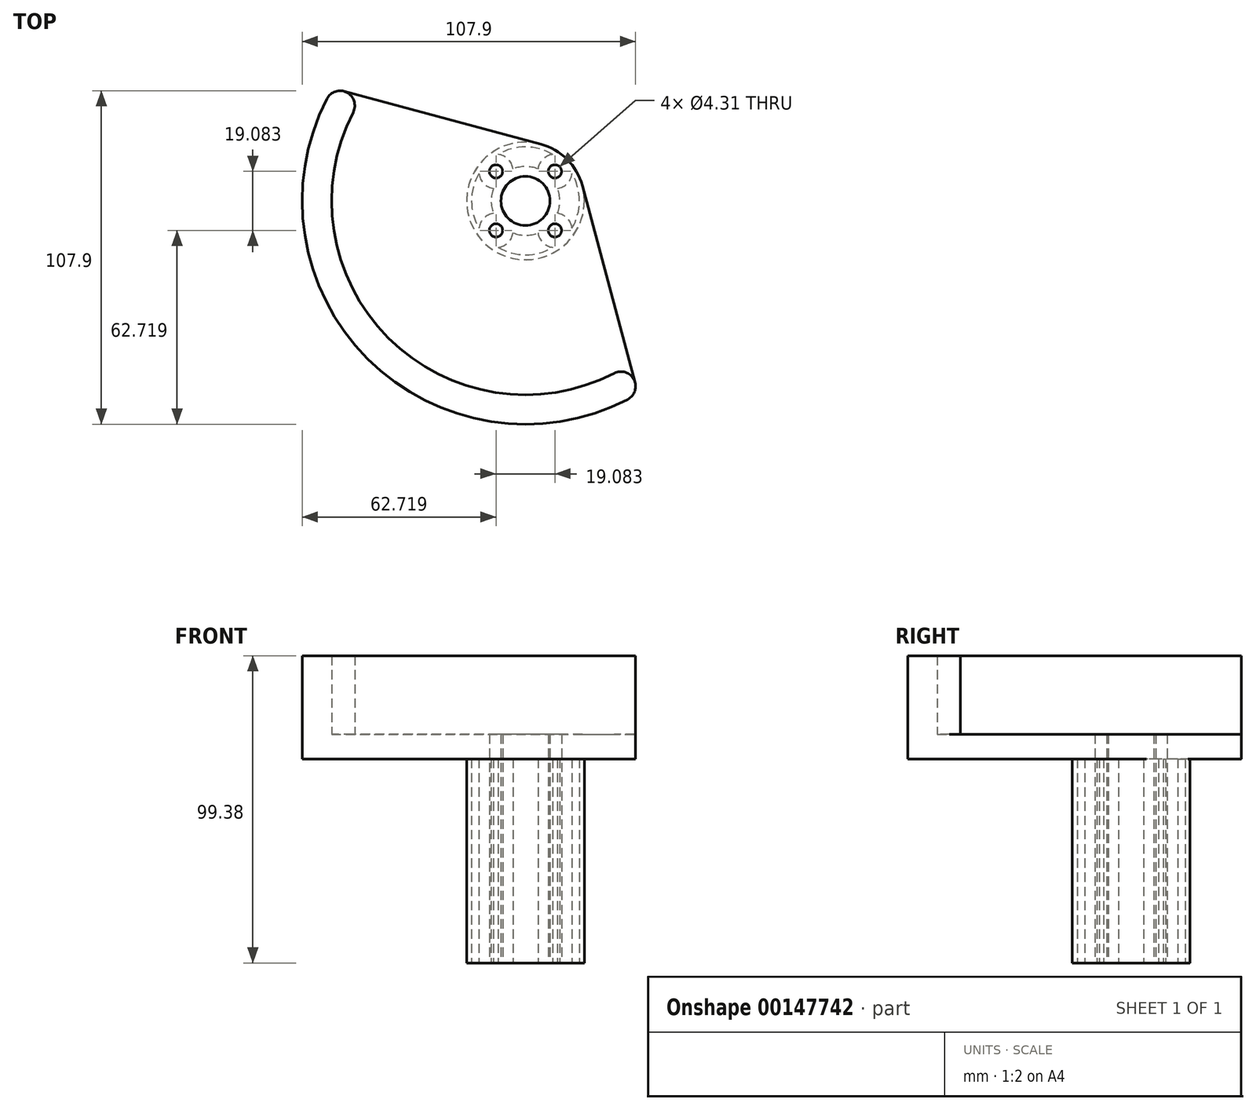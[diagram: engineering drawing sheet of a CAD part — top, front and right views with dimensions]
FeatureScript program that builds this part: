
annotation { "Feature Type Name" : "Feature", "Feature Type Description" : "" }
export const myFeature = defineFeature(function(context is Context, id is Id, definition is map)
    precondition{}
    {
        {
            var Q0;
            Q0=qCreatedBy(makeId("Top.planeOp"),FACE);
            var sketch = newSketch(context, id + "F0", { "sketchPlane" : qUnion([Q0])});
            skCircle(sketch, "E0", {"center": v(0, 0) * mm, "radius": 7.94 * mm});
            skLineSegment(sketch, "E1.bottom", {"start": v(9.54, 9.54) * mm, "end": v(-9.54, 9.54) * mm, "construction": true});
            skLineSegment(sketch, "E1.top", {"start": v(9.54, -9.54) * mm, "end": v(-9.54, -9.54) * mm, "construction": true});
            skLineSegment(sketch, "E1.left", {"start": v(9.54, 9.54) * mm, "end": v(9.54, -9.54) * mm, "construction": true});
            skLineSegment(sketch, "E1.right", {"start": v(-9.54, 9.54) * mm, "end": v(-9.54, -9.54) * mm, "construction": true});
            skCircle(sketch, "E2", {"center": v(-9.54, 9.54) * mm, "radius": 5.56 * mm, "construction": true});
            skLineSegment(sketch, "E3", {"start": v(0, 0) * mm, "end": v(0, 7.94) * mm});
            skCircle(sketch, "E4", {"center": v(-9.54, 9.54) * mm, "radius": 2.15 * mm});
            skCircle(sketch, "E5", {"center": v(-9.54, -9.54) * mm, "radius": 2.15 * mm});
            skCircle(sketch, "E6", {"center": v(9.54, -9.54) * mm, "radius": 2.15 * mm});
            skCircle(sketch, "E7", {"center": v(9.54, 9.54) * mm, "radius": 2.15 * mm});
            skCircle(sketch, "E8", {"center": v(0, 0) * mm, "radius": 19.05 * mm});
            skSolve(sketch);
        }
        {
            var Q0;
            Q0=qSketchRegion(id+"F0",true);
            extrude(context, id + "F1", {"entities" : qUnion([Q0]), "depth" : 66.04 * mm});
        }
        {
            var Q0;
            Q0=makeQuery(id+"F1.opExtrude","CAP_FACE",FACE,{"disambiguationData":[OSD([sQuery(id+"F0.wireOp",EDGE,"E0"),sQuery(id+"F0.wireOp",EDGE,"E4"),sQuery(id+"F0.wireOp",EDGE,"E5"),sQuery(id+"F0.wireOp",EDGE,"E6"),sQuery(id+"F0.wireOp",EDGE,"E7"),sQuery(id+"F0.wireOp",EDGE,"E8")])],"isStart":true});
            var sketch = newSketch(context, id + "F2", { "sketchPlane" : qUnion([Q0])});
            skArc(sketch, "E9", {"start": v(4.04, -10.35) * mm, "mid": v(5.65, -13.51) * mm, "end": v(8.85, -15.05) * mm});
            skArc(sketch, "E10", {"start": v(-8.85, -15.05) * mm, "mid": v(0, -17.46) * mm, "end": v(8.85, -15.05) * mm});
            skArc(sketch, "E11", {"start": v(-4.04, -10.35) * mm, "mid": v(0, -11.11) * mm, "end": v(4.04, -10.35) * mm});
            skArc(sketch, "E12", {"start": v(-8.85, -15.05) * mm, "mid": v(-5.65, -13.51) * mm, "end": v(-4.04, -10.35) * mm});
            skSolve(sketch);
        }
        {
            var Q0;
            Q0=qSketchRegion(id+"F2",true);
            var Q1;
            Q1=makeQuery(id+"F1.opExtrude","CAP_FACE",FACE,{"disambiguationData":[OSD([sQuery(id+"F0.wireOp",EDGE,"E0"),sQuery(id+"F0.wireOp",EDGE,"E4"),sQuery(id+"F0.wireOp",EDGE,"E5"),sQuery(id+"F0.wireOp",EDGE,"E6"),sQuery(id+"F0.wireOp",EDGE,"E7"),sQuery(id+"F0.wireOp",EDGE,"E8")])],"isStart":false});
            extrude(context, id + "F3", {"entities" : qUnion([Q0]), "operationType" : NewBodyOperationType.REMOVE, "endBound" : BoundingType.UP_TO_SURFACE, "oppositeDirection" : true, "endBoundEntityFace" : qUnion([Q1]), "depth" : 25.4 * mm});
        }
        {
            var Q0;
            Q0=makeQuery(id+"F3.boolean.opBoolean","COPY",FACE,{"derivedFrom":makeQuery(id+"F3.opExtrude","SWEPT_FACE",FACE,{"disambiguationData":[OSD([sQuery(id+"F2.wireOp",EDGE,"E10")])]})});
            var Q1;
            Q1=makeQuery(id+"F3.boolean.opBoolean","COPY",FACE,{"derivedFrom":makeQuery(id+"F3.opExtrude","SWEPT_FACE",FACE,{"disambiguationData":[OSD([sQuery(id+"F2.wireOp",EDGE,"E12")])]})});
            var Q2;
            Q2=makeQuery(id+"F3.boolean.opBoolean","COPY",FACE,{"derivedFrom":makeQuery(id+"F3.opExtrude","SWEPT_FACE",FACE,{"disambiguationData":[OSD([sQuery(id+"F2.wireOp",EDGE,"E11")])]})});
            var Q3;
            Q3=makeQuery(id+"F3.boolean.opBoolean","COPY",FACE,{"derivedFrom":makeQuery(id+"F3.opExtrude","SWEPT_FACE",FACE,{"disambiguationData":[OSD([sQuery(id+"F2.wireOp",EDGE,"E9")])]})});
            var Q4;
            Q4=makeQuery(id+"F1.opExtrude","SWEPT_FACE",FACE,{"disambiguationData":[OSD([sQuery(id+"F0.wireOp",EDGE,"E8")])]});
            circularPattern(context, id + "F4", {"patternType" : PatternType.FACE, "faces" : qUnion([Q0, Q1, Q2, Q3]), "axis" : qUnion([Q4]), "angle" : 90 * degree, "instanceCount" : 4});
        }
        {
            var Q0;
            Q0=makeQuery(id+"F1.opExtrude","CAP_FACE",FACE,{"disambiguationData":[OSD([sQuery(id+"F0.wireOp",EDGE,"E0"),sQuery(id+"F0.wireOp",EDGE,"E4"),sQuery(id+"F0.wireOp",EDGE,"E5"),sQuery(id+"F0.wireOp",EDGE,"E6"),sQuery(id+"F0.wireOp",EDGE,"E7"),sQuery(id+"F0.wireOp",EDGE,"E8")])],"isStart":false});
            var sketch = newSketch(context, id + "F5", { "sketchPlane" : qUnion([Q0])});
            skArc(sketch, "E13", {"start": v(18.4, 4.93) * mm, "mid": v(13.47, 13.47) * mm, "end": v(4.93, 18.4) * mm});
            skLineSegment(sketch, "E14", {"start": v(18.4, 4.93) * mm, "end": v(35.47, -58.79) * mm});
            skLineSegment(sketch, "E15", {"start": v(4.93, 18.4) * mm, "end": v(-58.79, 35.47) * mm});
            skLineSegment(sketch, "E16", {"start": v(4.93, 18.4) * mm, "end": v(-26.93, 18.4) * mm, "construction": true});
            skLineSegment(sketch, "E17", {"start": v(-26.93, 18.4) * mm, "end": v(-26.93, 26.94) * mm, "construction": true});
            skArc(sketch, "E18", {"start": v(-58.79, 35.47) * mm, "mid": v(-61.95, 35.23) * mm, "end": v(-64.25, 33.05) * mm});
            skArc(sketch, "E19", {"start": v(33.05, -64.25) * mm, "mid": v(35.23, -61.95) * mm, "end": v(35.47, -58.79) * mm});
            skArc(sketch, "E20", {"start": v(-64.25, 33.05) * mm, "mid": v(-51.1, -51.1) * mm, "end": v(33.05, -64.25) * mm});
            skLineSegment(sketch, "E21", {"start": v(18.4, 4.93) * mm, "end": v(18.4, -26.93) * mm, "construction": true});
            skLineSegment(sketch, "E22", {"start": v(18.4, -26.93) * mm, "end": v(26.94, -26.93) * mm, "construction": true});
            skCircle(sketch, "E23", {"center": v(-9.54, 9.54) * mm, "radius": 2.15 * mm});
            skCircle(sketch, "E24", {"center": v(9.54, 9.54) * mm, "radius": 2.15 * mm});
            skCircle(sketch, "E25", {"center": v(-9.54, -9.54) * mm, "radius": 2.15 * mm});
            skCircle(sketch, "E26", {"center": v(9.54, -9.54) * mm, "radius": 2.15 * mm});
            skCircle(sketch, "E27", {"center": v(0, 0) * mm, "radius": 7.94 * mm});
            skSolve(sketch);
        }
        {
            var Q0;
            Q0=qSketchRegion(id+"F5",true);
            extrude(context, id + "F6", {"entities" : qUnion([Q0]), "operationType" : NewBodyOperationType.ADD, "depth" : 7.94 * mm});
        }
        {
            var Q0;
            Q0=makeQuery(id+"F6.opExtrude","CAP_FACE",FACE,{"disambiguationData":[OSD([sQuery(id+"F5.wireOp",EDGE,"E13"),sQuery(id+"F5.wireOp",EDGE,"E14"),sQuery(id+"F5.wireOp",EDGE,"E15"),sQuery(id+"F5.wireOp",EDGE,"E18"),sQuery(id+"F5.wireOp",EDGE,"E19"),sQuery(id+"F5.wireOp",EDGE,"E20"),sQuery(id+"F5.wireOp",EDGE,"E23"),sQuery(id+"F5.wireOp",EDGE,"E24"),sQuery(id+"F5.wireOp",EDGE,"E25"),sQuery(id+"F5.wireOp",EDGE,"E26"),sQuery(id+"F5.wireOp",EDGE,"E27")])],"isStart":false});
            var sketch = newSketch(context, id + "F7", { "sketchPlane" : qUnion([Q0])});
            skArc(sketch, "E28", {"start": v(-64.25, 33.05) * mm, "mid": v(-51.1, -51.1) * mm, "end": v(33.05, -64.25) * mm});
            skArc(sketch, "E29", {"start": v(-55.78, 28.7) * mm, "mid": v(-57.84, 35.1) * mm, "end": v(-64.25, 33.05) * mm});
            skArc(sketch, "E30", {"start": v(33.05, -64.25) * mm, "mid": v(35.1, -57.84) * mm, "end": v(28.7, -55.78) * mm});
            skArc(sketch, "E31", {"start": v(-55.78, 28.7) * mm, "mid": v(-44.36, -44.36) * mm, "end": v(28.7, -55.78) * mm});
            skSolve(sketch);
        }
        {
            var Q0;
            Q0=qSketchRegion(id+"F7",true);
            extrude(context, id + "F8", {"entities" : qUnion([Q0]), "operationType" : NewBodyOperationType.ADD, "depth" : 25.4 * mm});
        }
    });
